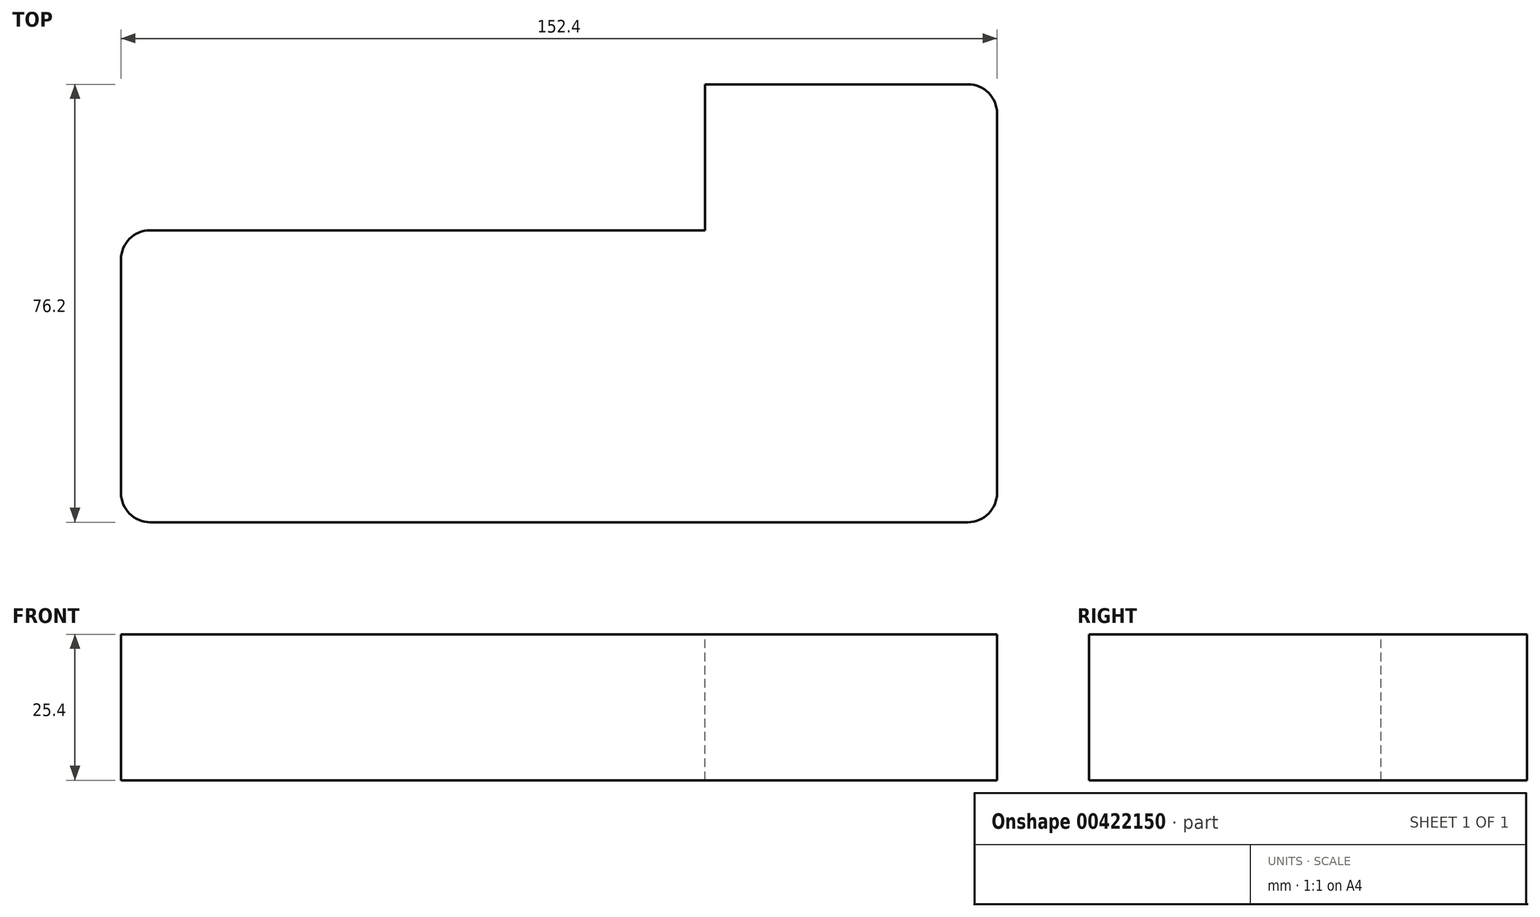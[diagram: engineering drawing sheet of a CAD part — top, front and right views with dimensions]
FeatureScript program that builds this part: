
annotation { "Feature Type Name" : "Feature", "Feature Type Description" : "" }
export const myFeature = defineFeature(function(context is Context, id is Id, definition is map)
    precondition{}
    {
        {
            var Q0;
            Q0=qCreatedBy(makeId("Top.planeOp"),FACE);
            var sketch = newSketch(context, id + "F0", { "sketchPlane" : qUnion([Q0])});
            skLineSegment(sketch, "E0", {"start": v(0, 0) * mm, "end": v(152.4, 0) * mm});
            skLineSegment(sketch, "E1", {"start": v(0, 0) * mm, "end": v(0, 50.8) * mm});
            skLineSegment(sketch, "E2", {"start": v(0, 50.8) * mm, "end": v(101.6, 50.8) * mm});
            skLineSegment(sketch, "E3", {"start": v(101.6, 50.8) * mm, "end": v(101.6, 76.2) * mm});
            skLineSegment(sketch, "E4", {"start": v(101.6, 76.2) * mm, "end": v(152.4, 76.2) * mm});
            skLineSegment(sketch, "E5", {"start": v(152.4, 76.2) * mm, "end": v(152.4, 0) * mm});
            skSolve(sketch);
        }
        {
            var Q0;
            Q0 = qSketchRegion(id + "F0", true);
            extrude(context, id + "F1", {"entities" : qUnion([Q0]), "oppositeDirection" : true, "depth" : 25.4 * mm});
        }
        {
            var Q0;
            Q0=makeQuery(id+"F1.opExtrude","SWEPT_EDGE",EDGE,{"disambiguationData":[OSD([sQuery(id+"F0.wireOp",EDGE,"E4"),sQuery(id+"F0.wireOp",EDGE,"E5")])]});
            fillet(context, id + "F2", {"entities" : qUnion([Q0]), "radius" : 5.08 * mm, "tangentPropagation" : true, "allowEdgeOverflow" : false});
        }
        {
            var Q0;
            Q0=makeQuery(id+"F1.opExtrude","SWEPT_EDGE",EDGE,{"disambiguationData":[OSD([sQuery(id+"F0.wireOp",EDGE,"E1"),sQuery(id+"F0.wireOp",EDGE,"E2")])]});
            fillet(context, id + "F3", {"entities" : qUnion([Q0]), "radius" : 5.08 * mm, "tangentPropagation" : true, "allowEdgeOverflow" : false});
        }
        {
            var Q0;
            Q0=makeQuery(id+"F1.opExtrude","SWEPT_EDGE",EDGE,{"disambiguationData":[OSD([sQuery(id+"F0.wireOp",EDGE,"E0"),sQuery(id+"F0.wireOp",EDGE,"E1")])]});
            fillet(context, id + "F4", {"entities" : qUnion([Q0]), "radius" : 5.08 * mm, "tangentPropagation" : true, "allowEdgeOverflow" : false});
        }
        {
            var Q0;
            Q0=makeQuery(id+"F1.opExtrude","SWEPT_EDGE",EDGE,{"disambiguationData":[OSD([sQuery(id+"F0.wireOp",EDGE,"E0"),sQuery(id+"F0.wireOp",EDGE,"E5")])]});
            fillet(context, id + "F5", {"entities" : qUnion([Q0]), "radius" : 5.08 * mm, "tangentPropagation" : true, "allowEdgeOverflow" : false});
        }
    });
